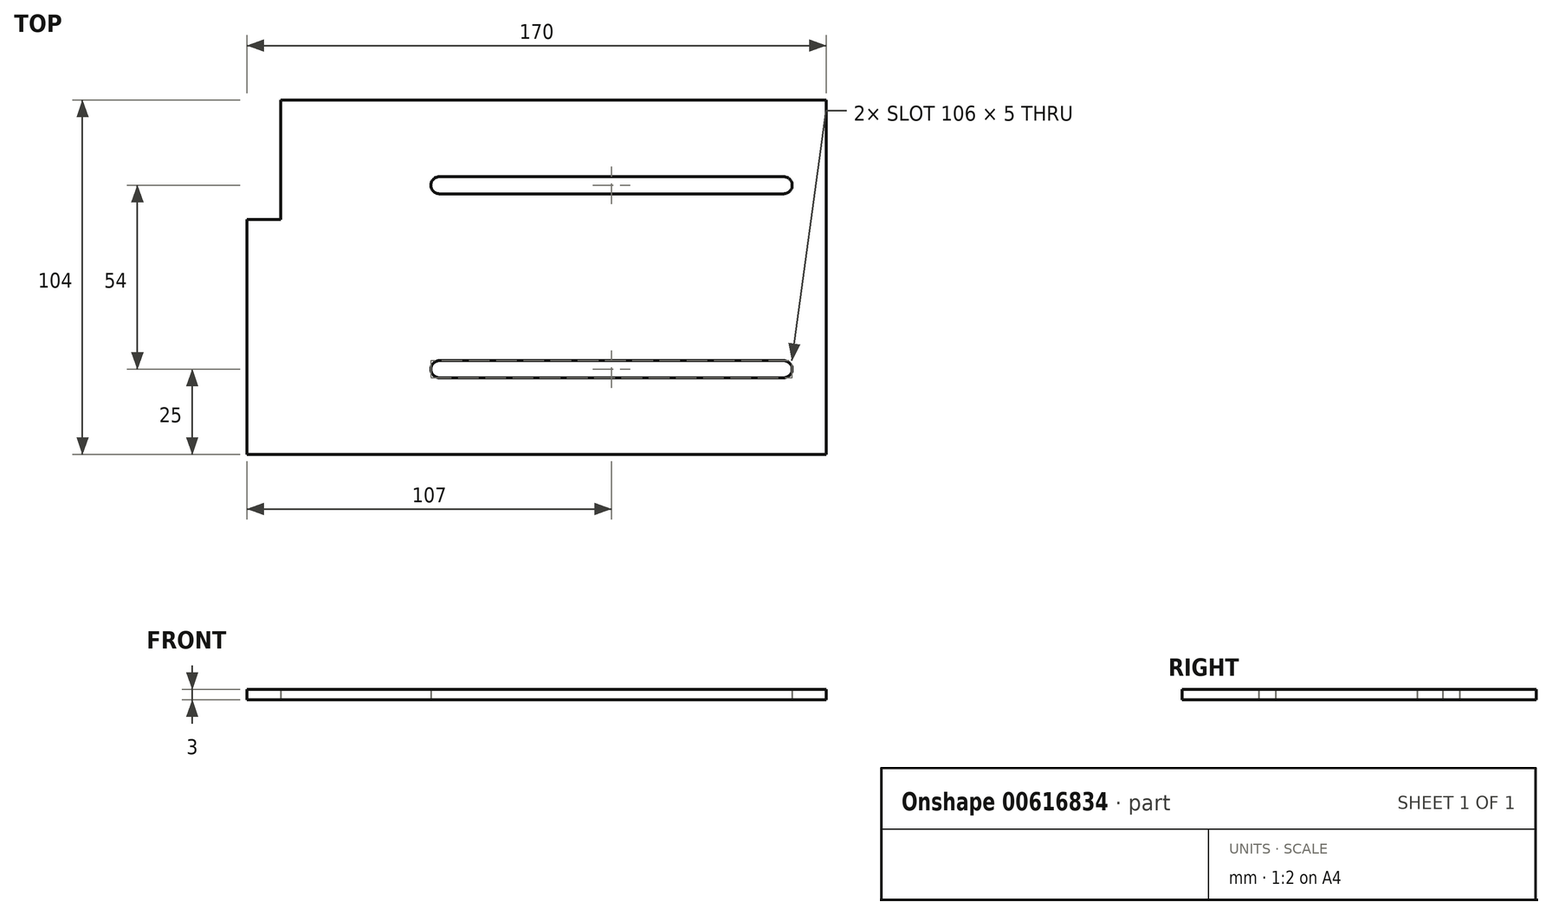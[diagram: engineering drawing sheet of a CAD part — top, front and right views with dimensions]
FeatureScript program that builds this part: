
annotation { "Feature Type Name" : "Feature", "Feature Type Description" : "" }
export const myFeature = defineFeature(function(context is Context, id is Id, definition is map)
    precondition{}
    {
        {
            var Q0;
            Q0=qCreatedBy(makeId("Top.planeOp"),FACE);
            var sketch = newSketch(context, id + "F0", { "sketchPlane" : qUnion([Q0])});
            skLineSegment(sketch, "E0.bottom", {"start": v(-75, 52) * mm, "end": v(85, 52) * mm});
            skLineSegment(sketch, "E0.top", {"start": v(-85, -52) * mm, "end": v(85, -52) * mm});
            skLineSegment(sketch, "E0.left", {"start": v(-85, 17) * mm, "end": v(-85, -52) * mm});
            skLineSegment(sketch, "E0.right", {"start": v(85, 52) * mm, "end": v(85, -52) * mm});
            skPoint(sketch, "E0.middle", {"position": v(0, 0) * mm});
            skLineSegment(sketch, "E1", {"start": v(-75, 52) * mm, "end": v(-75, 17) * mm});
            skLineSegment(sketch, "E2", {"start": v(-75, 17) * mm, "end": v(-85, 17) * mm});
            skLineSegment(sketch, "E3.bottom", {"start": v(72.5, 29.5) * mm, "end": v(-28.5, 29.5) * mm});
            skLineSegment(sketch, "E3.top", {"start": v(72.5, 24.5) * mm, "end": v(-28.5, 24.5) * mm});
            skPoint(sketch, "E3.middle", {"position": v(22, 27) * mm});
            skArc(sketch, "E4", {"start": v(-28.5, 29.5) * mm, "mid": v(-31, 27) * mm, "end": v(-28.5, 24.5) * mm});
            skArc(sketch, "E5", {"start": v(72.5, 24.5) * mm, "mid": v(75, 27) * mm, "end": v(72.5, 29.5) * mm});
            skPoint(sketch, "E6.orphan", {"position": v(-85, 52) * mm});
            skLineSegment(sketch, "E7.MirrorCS", {"start": v(72.5, -29.5) * mm, "end": v(-28.5, -29.5) * mm});
            skLineSegment(sketch, "E8.MirrorCS", {"start": v(72.5, -24.5) * mm, "end": v(-28.5, -24.5) * mm});
            skArc(sketch, "E9.MirrorCS", {"start": v(-28.5, -29.5) * mm, "mid": v(-31, -27) * mm, "end": v(-28.5, -24.5) * mm});
            skArc(sketch, "E10.MirrorCS", {"start": v(72.5, -24.5) * mm, "mid": v(75, -27) * mm, "end": v(72.5, -29.5) * mm});
            skSolve(sketch);
        }
        {
            var Q0;
            Q0 = qSketchRegion(id + "F0", true);
            extrude(context, id + "F1", {"entities" : qUnion([Q0]), "depth" : 3 * mm, "offsetDistance" : 25 * mm});
        }
    });
